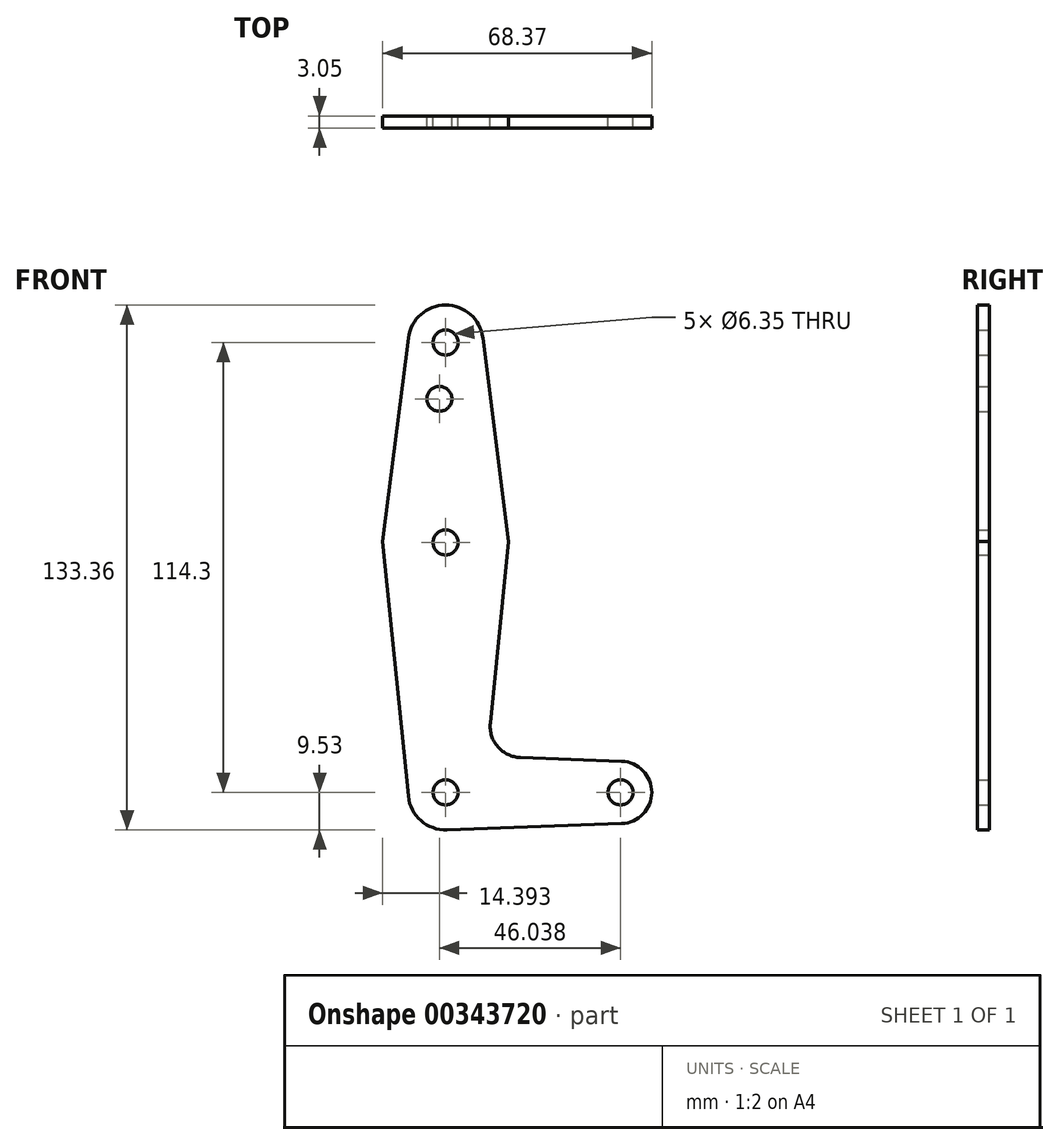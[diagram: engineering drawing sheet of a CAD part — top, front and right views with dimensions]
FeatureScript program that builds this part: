
annotation { "Feature Type Name" : "Feature", "Feature Type Description" : "" }
export const myFeature = defineFeature(function(context is Context, id is Id, definition is map)
    precondition{}
    {
        {
            var Q0;
            Q0=qCreatedBy(makeId("Front.planeOp"),FACE);
            var sketch = newSketch(context, id + "F0", { "sketchPlane" : qUnion([Q0])});
            skLineSegment(sketch, "E0", {"start": v(0, 0) * mm, "end": v(0, 114.3) * mm, "construction": true});
            skLineSegment(sketch, "E1", {"start": v(44.45, 0) * mm, "end": v(0, 0) * mm, "construction": true});
            skCircle(sketch, "E2", {"center": v(0, 114.3) * mm, "radius": 9.53 * mm});
            skCircle(sketch, "E3", {"center": v(0, 0) * mm, "radius": 9.53 * mm});
            skCircle(sketch, "E4", {"center": v(44.45, 0) * mm, "radius": 7.94 * mm});
            skCircle(sketch, "E5", {"center": v(0, 63.5) * mm, "radius": 15.88 * mm});
            skLineSegment(sketch, "E6", {"start": v(-9.45, 115.5) * mm, "end": v(-15.98, 63.7) * mm});
            skLineSegment(sketch, "E7", {"start": v(15.98, 63.7) * mm, "end": v(11.34, 17.6) * mm});
            skLineSegment(sketch, "E8", {"start": v(-15.98, 63.7) * mm, "end": v(-9.48, -0.95) * mm});
            skLineSegment(sketch, "E9", {"start": v(18.97, 8.85) * mm, "end": v(44.73, 7.93) * mm});
            skLineSegment(sketch, "E10", {"start": v(0.34, -9.52) * mm, "end": v(44.73, -7.93) * mm});
            skLineSegment(sketch, "E11", {"start": v(9.45, 115.5) * mm, "end": v(15.98, 63.7) * mm});
            skCircle(sketch, "E12", {"center": v(0, 114.3) * mm, "radius": 3.18 * mm});
            skCircle(sketch, "E13", {"center": v(0, 63.5) * mm, "radius": 3.18 * mm});
            skCircle(sketch, "E14", {"center": v(-1.59, 100) * mm, "radius": 3.18 * mm});
            skCircle(sketch, "E15", {"center": v(0, 0) * mm, "radius": 3.18 * mm});
            skCircle(sketch, "E16", {"center": v(44.45, 0) * mm, "radius": 3.18 * mm});
            skArc(sketch, "E17.filletArc", {"start": v(11.34, 17.6) * mm, "mid": v(13.26, 11.57) * mm, "end": v(18.97, 8.85) * mm});
            skSolve(sketch);
        }
        {
            var Q0;
            Q0 = qSketchRegion(id + "F0", true);
            extrude(context, id + "F1", {"entities" : qUnion([Q0]), "depth" : 3.05 * mm});
        }
    });
